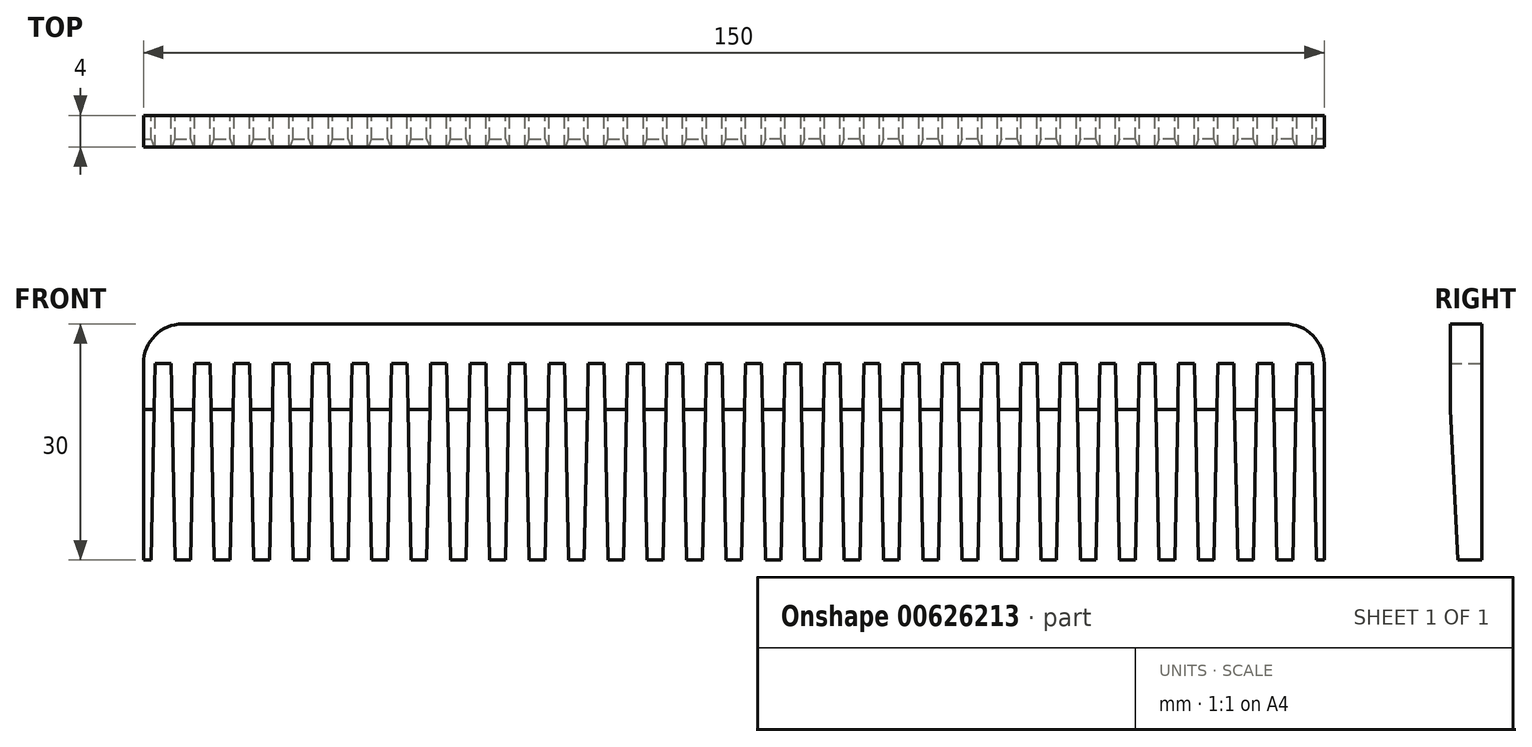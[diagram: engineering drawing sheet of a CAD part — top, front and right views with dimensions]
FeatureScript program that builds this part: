
annotation { "Feature Type Name" : "Feature", "Feature Type Description" : "" }
export const myFeature = defineFeature(function(context is Context, id is Id, definition is map)
    precondition{}
    {
        {
            var Q0;
            Q0=qCreatedBy(makeId("Front.planeOp"),FACE);
            var sketch = newSketch(context, id + "F0", { "sketchPlane" : qUnion([Q0])});
            skLineSegment(sketch, "E0", {"start": v(-75, 0) * mm, "end": v(-75, 30) * mm});
            skLineSegment(sketch, "E1", {"start": v(-75, 30) * mm, "end": v(0, 30) * mm});
            skLineSegment(sketch, "E2", {"start": v(0, 30) * mm, "end": v(0, 0) * mm});
            skLineSegment(sketch, "E3", {"start": v(0, 0) * mm, "end": v(-75, 0) * mm});
            skLineSegment(sketch, "E4", {"start": v(-74, 0) * mm, "end": v(-73.5, 25) * mm});
            skLineSegment(sketch, "E5", {"start": v(-73.5, 25) * mm, "end": v(-71.5, 25) * mm});
            skLineSegment(sketch, "E6", {"start": v(-71.5, 25) * mm, "end": v(-71, 0) * mm});
            skLineSegment(sketch, "E7", {"start": v(-72.5, 25) * mm, "end": v(-72.5, 1.14) * mm, "construction": true});
            skLineSegment(sketch, "E8.1.0.0", {"start": v(-66.5, 25) * mm, "end": v(-66, 0) * mm});
            skLineSegment(sketch, "E8.1.0.1", {"start": v(-69, 0) * mm, "end": v(-68.5, 25) * mm});
            skLineSegment(sketch, "E8.1.0.2", {"start": v(-68.5, 25) * mm, "end": v(-66.5, 25) * mm});
            skLineSegment(sketch, "E8.2.0.0", {"start": v(-61.5, 25) * mm, "end": v(-61, 0) * mm});
            skLineSegment(sketch, "E8.2.0.1", {"start": v(-64, 0) * mm, "end": v(-63.5, 25) * mm});
            skLineSegment(sketch, "E8.2.0.2", {"start": v(-63.5, 25) * mm, "end": v(-61.5, 25) * mm});
            skLineSegment(sketch, "E8.3.0.0", {"start": v(-56.5, 25) * mm, "end": v(-56, 0) * mm});
            skLineSegment(sketch, "E8.3.0.1", {"start": v(-59, 0) * mm, "end": v(-58.5, 25) * mm});
            skLineSegment(sketch, "E8.3.0.2", {"start": v(-58.5, 25) * mm, "end": v(-56.5, 25) * mm});
            skLineSegment(sketch, "E8.4.0.0", {"start": v(-51.5, 25) * mm, "end": v(-51, 0) * mm});
            skLineSegment(sketch, "E8.4.0.1", {"start": v(-54, 0) * mm, "end": v(-53.5, 25) * mm});
            skLineSegment(sketch, "E8.4.0.2", {"start": v(-53.5, 25) * mm, "end": v(-51.5, 25) * mm});
            skLineSegment(sketch, "E8.5.0.0", {"start": v(-46.5, 25) * mm, "end": v(-46, 0) * mm});
            skLineSegment(sketch, "E8.5.0.1", {"start": v(-49, 0) * mm, "end": v(-48.5, 25) * mm});
            skLineSegment(sketch, "E8.5.0.2", {"start": v(-48.5, 25) * mm, "end": v(-46.5, 25) * mm});
            skLineSegment(sketch, "E8.6.0.0", {"start": v(-41.5, 25) * mm, "end": v(-41, 0) * mm});
            skLineSegment(sketch, "E8.6.0.1", {"start": v(-44, 0) * mm, "end": v(-43.5, 25) * mm});
            skLineSegment(sketch, "E8.6.0.2", {"start": v(-43.5, 25) * mm, "end": v(-41.5, 25) * mm});
            skLineSegment(sketch, "E8.7.0.0", {"start": v(-36.5, 25) * mm, "end": v(-36, 0) * mm});
            skLineSegment(sketch, "E8.7.0.1", {"start": v(-39, 0) * mm, "end": v(-38.5, 25) * mm});
            skLineSegment(sketch, "E8.7.0.2", {"start": v(-38.5, 25) * mm, "end": v(-36.5, 25) * mm});
            skLineSegment(sketch, "E8.8.0.0", {"start": v(-31.5, 25) * mm, "end": v(-31, 0) * mm});
            skLineSegment(sketch, "E8.8.0.1", {"start": v(-34, 0) * mm, "end": v(-33.5, 25) * mm});
            skLineSegment(sketch, "E8.8.0.2", {"start": v(-33.5, 25) * mm, "end": v(-31.5, 25) * mm});
            skLineSegment(sketch, "E8.9.0.0", {"start": v(-26.5, 25) * mm, "end": v(-26, 0) * mm});
            skLineSegment(sketch, "E8.9.0.1", {"start": v(-29, 0) * mm, "end": v(-28.5, 25) * mm});
            skLineSegment(sketch, "E8.9.0.2", {"start": v(-28.5, 25) * mm, "end": v(-26.5, 25) * mm});
            skLineSegment(sketch, "E8.10.0.0", {"start": v(-21.5, 25) * mm, "end": v(-21, 0) * mm});
            skLineSegment(sketch, "E8.10.0.1", {"start": v(-24, 0) * mm, "end": v(-23.5, 25) * mm});
            skLineSegment(sketch, "E8.10.0.2", {"start": v(-23.5, 25) * mm, "end": v(-21.5, 25) * mm});
            skLineSegment(sketch, "E8.11.0.0", {"start": v(-16.5, 25) * mm, "end": v(-16, 0) * mm});
            skLineSegment(sketch, "E8.11.0.1", {"start": v(-19, 0) * mm, "end": v(-18.5, 25) * mm});
            skLineSegment(sketch, "E8.11.0.2", {"start": v(-18.5, 25) * mm, "end": v(-16.5, 25) * mm});
            skLineSegment(sketch, "E8.12.0.0", {"start": v(-11.5, 25) * mm, "end": v(-11, 0) * mm});
            skLineSegment(sketch, "E8.12.0.1", {"start": v(-14, 0) * mm, "end": v(-13.5, 25) * mm});
            skLineSegment(sketch, "E8.12.0.2", {"start": v(-13.5, 25) * mm, "end": v(-11.5, 25) * mm});
            skLineSegment(sketch, "E8.13.0.0", {"start": v(-6.5, 25) * mm, "end": v(-6, 0) * mm});
            skLineSegment(sketch, "E8.13.0.1", {"start": v(-9, 0) * mm, "end": v(-8.5, 25) * mm});
            skLineSegment(sketch, "E8.13.0.2", {"start": v(-8.5, 25) * mm, "end": v(-6.5, 25) * mm});
            skLineSegment(sketch, "E8.14.0.0", {"start": v(-1.5, 25) * mm, "end": v(-1, 0) * mm});
            skLineSegment(sketch, "E8.14.0.1", {"start": v(-4, 0) * mm, "end": v(-3.5, 25) * mm});
            skLineSegment(sketch, "E8.14.0.2", {"start": v(-3.5, 25) * mm, "end": v(-1.5, 25) * mm});
            skLineSegment(sketch, "E8.direction1", {"start": v(-74, 0) * mm, "end": v(-69, 0) * mm, "construction": true});
            skSolve(sketch);
        }
        {
            var Q0;
            {var subQ25=sQuery(id+"F0.wireOp",EDGE,"E0");Q0=makeQuery(id+"F0.imprint","IMPRINT",FACE,{"disambiguationData":[TD([[makeQuery(id+"F0.imprint","IMPRINT",EDGE,{"derivedFrom":subQ25}),-1.0]])]});}
            extrude(context, id + "F1", {"entities" : qUnion([Q0]), "endBound" : BoundingType.SYMMETRIC, "depth" : 4 * mm, "offsetDistance" : 25 * mm});
        }
        {
            var Q0;
            Q0=makeQuery(id+"F1.opExtrude","SWEPT_EDGE",EDGE,{"disambiguationData":[OSD([sQuery(id+"F0.wireOp",EDGE,"E0"),sQuery(id+"F0.wireOp",EDGE,"E1")])]});
            fillet(context, id + "F2", {"entities" : qUnion([Q0]), "radius" : 5 * mm, "tangentPropagation" : true, "allowEdgeOverflow" : false});
        }
        {
            var Q0;
            Q0=qCreatedBy(makeId("Right.planeOp"),FACE);
            var sketch = newSketch(context, id + "F3", { "sketchPlane" : qUnion([Q0])});
            skLineSegment(sketch, "E9", {"start": v(-2, 19.11) * mm, "end": v(-1.04, 0) * mm});
            skLineSegment(sketch, "E10", {"start": v(-1.04, 0) * mm, "end": v(-2, 0) * mm});
            skLineSegment(sketch, "E11", {"start": v(-2, 0) * mm, "end": v(-2, 19.11) * mm});
            skSolve(sketch);
        }
        {
            var Q0;
            Q0 = qSketchRegion(id + "F3", true);
            extrude(context, id + "F4", {"entities" : qUnion([Q0]), "operationType" : NewBodyOperationType.REMOVE, "oppositeDirection" : true, "depth" : 208 * mm, "offsetDistance" : 25 * mm});
        }
        {
            var Q0;
            Q0=makeQuery(id+"F1.opExtrude","SWEPT_BODY",BODY,{"disambiguationData":[OSD([sQuery(id+"F0.wireOp",EDGE,"E0"),sQuery(id+"F0.wireOp",EDGE,"E1"),sQuery(id+"F0.wireOp",EDGE,"E2"),sQuery(id+"F0.wireOp",EDGE,"E3"),sQuery(id+"F0.wireOp",EDGE,"E4"),sQuery(id+"F0.wireOp",EDGE,"E5"),sQuery(id+"F0.wireOp",EDGE,"E6"),sQuery(id+"F0.wireOp",EDGE,"E8.1.0.0"),sQuery(id+"F0.wireOp",EDGE,"E8.1.0.1"),sQuery(id+"F0.wireOp",EDGE,"E8.1.0.2"),sQuery(id+"F0.wireOp",EDGE,"E8.2.0.0"),sQuery(id+"F0.wireOp",EDGE,"E8.2.0.1"),sQuery(id+"F0.wireOp",EDGE,"E8.2.0.2"),sQuery(id+"F0.wireOp",EDGE,"E8.3.0.0"),sQuery(id+"F0.wireOp",EDGE,"E8.3.0.1"),sQuery(id+"F0.wireOp",EDGE,"E8.3.0.2"),sQuery(id+"F0.wireOp",EDGE,"E8.4.0.0"),sQuery(id+"F0.wireOp",EDGE,"E8.4.0.1"),sQuery(id+"F0.wireOp",EDGE,"E8.4.0.2"),sQuery(id+"F0.wireOp",EDGE,"E8.5.0.0"),sQuery(id+"F0.wireOp",EDGE,"E8.5.0.1"),sQuery(id+"F0.wireOp",EDGE,"E8.5.0.2"),sQuery(id+"F0.wireOp",EDGE,"E8.6.0.0"),sQuery(id+"F0.wireOp",EDGE,"E8.6.0.1"),sQuery(id+"F0.wireOp",EDGE,"E8.6.0.2"),sQuery(id+"F0.wireOp",EDGE,"E8.7.0.0"),sQuery(id+"F0.wireOp",EDGE,"E8.7.0.1"),sQuery(id+"F0.wireOp",EDGE,"E8.7.0.2"),sQuery(id+"F0.wireOp",EDGE,"E8.8.0.0"),sQuery(id+"F0.wireOp",EDGE,"E8.8.0.1"),sQuery(id+"F0.wireOp",EDGE,"E8.8.0.2"),sQuery(id+"F0.wireOp",EDGE,"E8.9.0.0"),sQuery(id+"F0.wireOp",EDGE,"E8.9.0.1"),sQuery(id+"F0.wireOp",EDGE,"E8.9.0.2"),sQuery(id+"F0.wireOp",EDGE,"E8.10.0.0"),sQuery(id+"F0.wireOp",EDGE,"E8.10.0.1"),sQuery(id+"F0.wireOp",EDGE,"E8.10.0.2"),sQuery(id+"F0.wireOp",EDGE,"E8.11.0.0"),sQuery(id+"F0.wireOp",EDGE,"E8.11.0.1"),sQuery(id+"F0.wireOp",EDGE,"E8.11.0.2"),sQuery(id+"F0.wireOp",EDGE,"E8.12.0.0"),sQuery(id+"F0.wireOp",EDGE,"E8.12.0.1"),sQuery(id+"F0.wireOp",EDGE,"E8.12.0.2"),sQuery(id+"F0.wireOp",EDGE,"E8.13.0.0"),sQuery(id+"F0.wireOp",EDGE,"E8.13.0.1"),sQuery(id+"F0.wireOp",EDGE,"E8.13.0.2"),sQuery(id+"F0.wireOp",EDGE,"E8.14.0.0"),sQuery(id+"F0.wireOp",EDGE,"E8.14.0.1"),sQuery(id+"F0.wireOp",EDGE,"E8.14.0.2")])]});
            var Q1;
            Q1=makeQuery(id+"F1.opExtrude","SWEPT_FACE",FACE,{"disambiguationData":[OSD([sQuery(id+"F0.wireOp",EDGE,"E2")])]});
            mirror(context, id + "F5", {"operationType" : NewBodyOperationType.ADD, "entities" : qUnion([Q0]), "mirrorPlane" : qUnion([Q1])});
        }
    });
